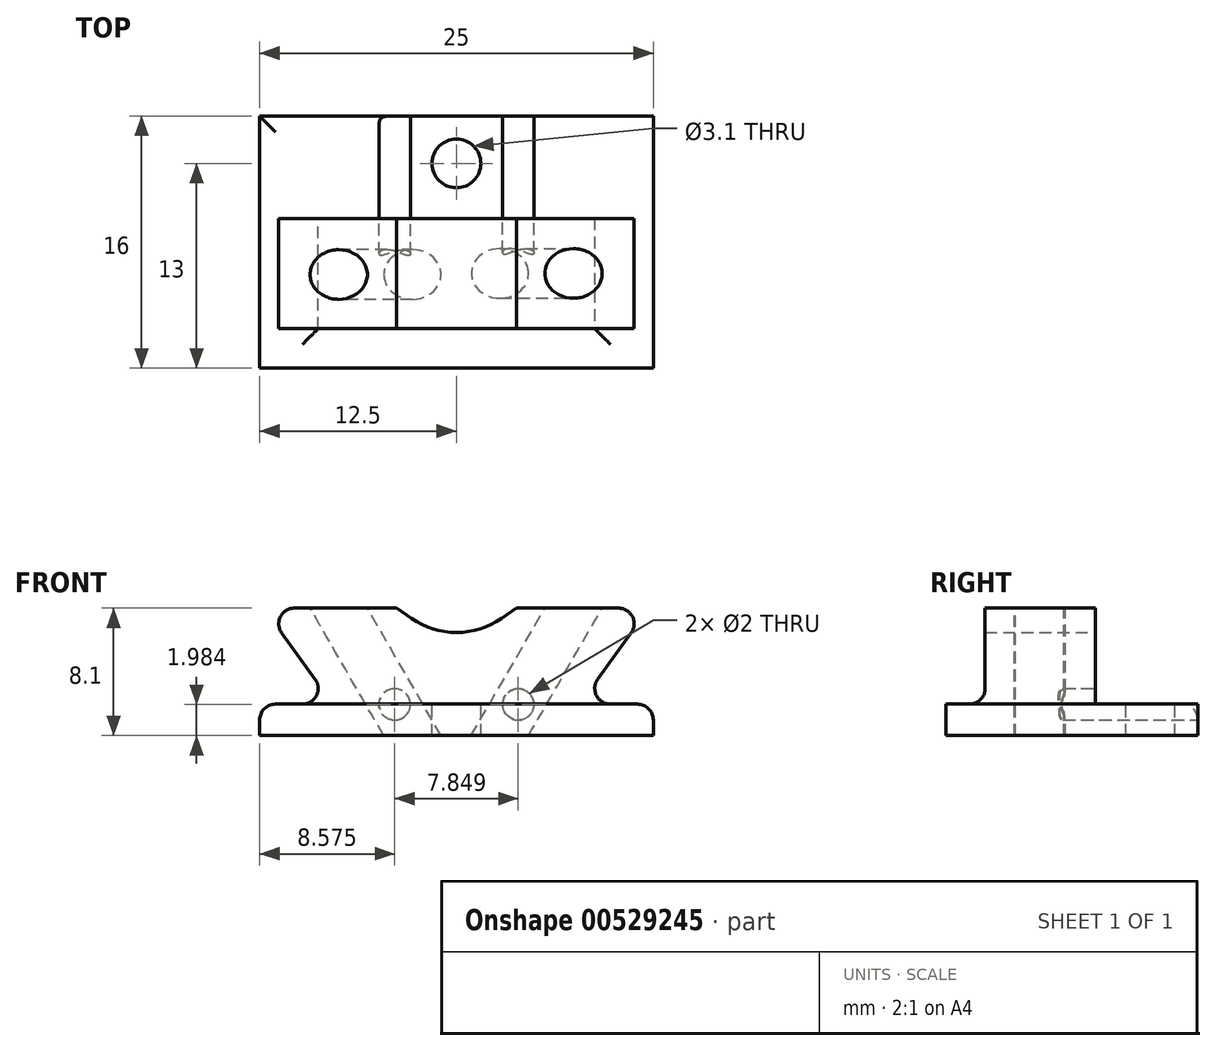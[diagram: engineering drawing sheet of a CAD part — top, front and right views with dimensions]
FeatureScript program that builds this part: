
annotation { "Feature Type Name" : "Feature", "Feature Type Description" : "" }
export const myFeature = defineFeature(function(context is Context, id is Id, definition is map)
    precondition{}
    {
        {
            var Q0;
            Q0=qCreatedBy(makeId("Front.planeOp"),FACE);
            cPlane(context, id + "F0", {"entities" : qUnion([Q0]), "cplaneType" : CPlaneType.OFFSET, "offset" : 2 * mm, "width" : 150 * mm, "height" : 150 * mm});
        }
        {
            var Q0;
            Q0=qCreatedBy(makeId("Top.planeOp"),FACE);
            var sketch = newSketch(context, id + "F1", { "sketchPlane" : qUnion([Q0])});
            skLineSegment(sketch, "E0.rect.bottom", {"start": v(12.5, -8) * mm, "end": v(-12.5, -8) * mm});
            skLineSegment(sketch, "E0.rect.top", {"start": v(12.5, 8) * mm, "end": v(-12.5, 8) * mm});
            skLineSegment(sketch, "E0.rect.left", {"start": v(12.5, -8) * mm, "end": v(12.5, 8) * mm});
            skLineSegment(sketch, "E0.rect.right", {"start": v(-12.5, -8) * mm, "end": v(-12.5, 8) * mm});
            skPoint(sketch, "E0.rect.middle", {"position": v(0, 0) * mm});
            skSolve(sketch);
        }
        {
            var Q0;
            Q0=makeQuery(id+"F1.imprint","IMPRINT",FACE,{"disambiguationData":[TD([[makeQuery(id+"F1.imprint","IMPRINT",EDGE,{"derivedFrom":sQuery(id+"F1.wireOp",EDGE,"E0.rect.bottom")}),-1.0]])]});
            extrude(context, id + "F2", {"entities" : qUnion([Q0]), "depth" : 2 * mm});
        }
        {
            var Q0;
            Q0=makeQuery(id+"F2.opExtrude","CAP_FACE",FACE,{"disambiguationData":[OSD([sQuery(id+"F1.wireOp",EDGE,"E0.rect.bottom"),sQuery(id+"F1.wireOp",EDGE,"E0.rect.top"),sQuery(id+"F1.wireOp",EDGE,"E0.rect.left"),sQuery(id+"F1.wireOp",EDGE,"E0.rect.right")])],"isStart":false});
            var sketch = newSketch(context, id + "F3", { "sketchPlane" : qUnion([Q0])});
            skLineSegment(sketch, "E1", {"start": v(-17.25, 5) * mm, "end": v(20.16, 5) * mm, "construction": true});
            skCircle(sketch, "E2", {"center": v(0, 5) * mm, "radius": 1.55 * mm});
            skSolve(sketch);
        }
        {
            var Q0;
            Q0=makeQuery(id+"F3.imprint","IMPRINT",FACE,{"disambiguationData":[TD([[makeQuery(id+"F3.imprint","IMPRINT",EDGE,{"derivedFrom":sQuery(id+"F3.wireOp",EDGE,"E2")}),1.0]])]});
            extrude(context, id + "F4", {"entities" : qUnion([Q0]), "operationType" : NewBodyOperationType.REMOVE, "endBound" : BoundingType.THROUGH_ALL, "oppositeDirection" : true, "depth" : 25 * mm});
        }
        {
            var Q0;
            Q0=qCreatedBy(id+"F0.planeOp",FACE);
            var sketch = newSketch(context, id + "F5", { "sketchPlane" : qUnion([Q0])});
            skLineSegment(sketch, "E3", {"start": v(-12.25, 8.1) * mm, "end": v(-3.8, 8.1) * mm});
            skLineSegment(sketch, "E4", {"start": v(-3.8, 8.1) * mm, "end": v(-2.87, 7.45) * mm});
            skLineSegment(sketch, "E5", {"start": v(2.87, 7.45) * mm, "end": v(3.8, 8.1) * mm});
            skLineSegment(sketch, "E6", {"start": v(3.8, 8.1) * mm, "end": v(12.25, 8.1) * mm});
            skLineSegment(sketch, "E7", {"start": v(-12.25, 8.1) * mm, "end": v(-6.37, 0) * mm});
            skLineSegment(sketch, "E8", {"start": v(6.37, 0) * mm, "end": v(12.25, 8.1) * mm});
            skLineSegment(sketch, "E9", {"start": v(-6.37, 0) * mm, "end": v(6.37, 0) * mm});
            skPoint(sketch, "E10.orphan", {"position": v(0, -8.79) * mm});
            skPoint(sketch, "E11.visualSharp", {"position": v(0, 5.44) * mm});
            skArc(sketch, "E11.filletArc", {"start": v(-2.87, 7.45) * mm, "mid": v(0, 6.55) * mm, "end": v(2.87, 7.45) * mm});
            skSolve(sketch);
        }
        {
            var Q0;
            Q0=qSketchRegion(id+"F5",true);
            extrude(context, id + "F6", {"entities" : qUnion([Q0]), "operationType" : NewBodyOperationType.ADD, "endBound" : BoundingType.SYMMETRIC, "depth" : 7 * mm});
        }
        {
            var Q0;
            Q0=qCreatedBy(id+"F0.planeOp",FACE);
            var sketch = newSketch(context, id + "F7", { "sketchPlane" : qUnion([Q0])});
            skLineSegment(sketch, "E12", {"start": v(-10, 12.55) * mm, "end": v(0, -4.77) * mm, "construction": true});
            skLineSegment(sketch, "E13", {"start": v(0, -4.77) * mm, "end": v(10, 12.55) * mm, "construction": true});
            skLineSegment(sketch, "E14", {"start": v(10, 12.55) * mm, "end": v(-10, 12.55) * mm, "construction": true});
            skSolve(sketch);
        }
        {
            var Q0;
            Q0=sQuery(id+"F7.wireOp",VERTEX,"E14.start");
            var Q1;
            Q1=sQuery(id+"F7.wireOp",EDGE,"E13");
            cPlane(context, id + "F8", {"entities" : qUnion([Q0, Q1]), "cplaneType" : CPlaneType.LINE_POINT, "offset" : 150 * mm, "width" : 150 * mm, "height" : 150 * mm});
        }
        {
            var Q0;
            Q0=qCreatedBy(id+"F8.planeOp",FACE);
            var sketch = newSketch(context, id + "F9", { "sketchPlane" : qUnion([Q0])});
            skCircle(sketch, "E15", {"center": v(2.39, -2) * mm, "radius": 1.57 * mm});
            skSolve(sketch);
        }
        {
            var Q0;
            Q0=qSketchRegion(id+"F9",true);
            extrude(context, id + "F10", {"entities" : qUnion([Q0]), "operationType" : NewBodyOperationType.REMOVE, "oppositeDirection" : true, "depth" : 25 * mm});
        }
        {
            var Q0;
            Q0=sQuery(id+"F7.wireOp",EDGE,"E12");
            var Q1;
            Q1=sQuery(id+"F7.wireOp",VERTEX,"E14.end");
            cPlane(context, id + "F11", {"entities" : qUnion([Q0, Q1]), "cplaneType" : CPlaneType.LINE_POINT, "offset" : 150 * mm, "width" : 150 * mm, "height" : 150 * mm});
        }
        {
            var Q0;
            Q0=qCreatedBy(id+"F11.planeOp",FACE);
            var sketch = newSketch(context, id + "F12", { "sketchPlane" : qUnion([Q0])});
            skCircle(sketch, "E16", {"center": v(-2.42, 2.06) * mm, "radius": 1.57 * mm});
            skSolve(sketch);
        }
        {
            var Q0;
            Q0=qSketchRegion(id+"F12",true);
            extrude(context, id + "F13", {"entities" : qUnion([Q0]), "operationType" : NewBodyOperationType.REMOVE, "endBound" : BoundingType.THROUGH_ALL, "depth" : 25 * mm});
        }
        {
            var Q0;
            Q0=makeQuery(id+"F2.opExtrude","SWEPT_FACE",FACE,{"disambiguationData":[OSD([sQuery(id+"F1.wireOp",EDGE,"E0.rect.top")])]});
            var sketch = newSketch(context, id + "F14", { "sketchPlane" : qUnion([Q0])});
            skCircle(sketch, "E17", {"center": v(3.92, 1.98) * mm, "radius": 1 * mm});
            skCircle(sketch, "E18.0.MirrorC", {"center": v(-3.92, 1.98) * mm, "radius": 1 * mm});
            skSolve(sketch);
        }
        {
            var Q0;
            Q0=qSketchRegion(id+"F14",true);
            var Q1;
            Q1=qCreatedBy(id+"F0.planeOp",FACE);
            extrude(context, id + "F15", {"entities" : qUnion([Q0]), "operationType" : NewBodyOperationType.REMOVE, "endBound" : BoundingType.UP_TO_SURFACE, "oppositeDirection" : true, "endBoundEntityFace" : qUnion([Q1]), "depth" : 25 * mm});
        }
        {
            var Q0;
            Q0=makeQuery(id+"F6.boolean.opBoolean","INTERSECT",EDGE,{"derivedFrom":[makeQuery(id+"F2.opExtrude","CAP_FACE",FACE,{"disambiguationData":[OSD([sQuery(id+"F1.wireOp",EDGE,"E0.rect.bottom"),sQuery(id+"F1.wireOp",EDGE,"E0.rect.top"),sQuery(id+"F1.wireOp",EDGE,"E0.rect.left"),sQuery(id+"F1.wireOp",EDGE,"E0.rect.right")])],"isStart":false}),makeQuery(id+"F6.opExtrude","CAP_FACE",FACE,{"disambiguationData":[OSD([sQuery(id+"F5.wireOp",EDGE,"E3"),sQuery(id+"F5.wireOp",EDGE,"E4"),sQuery(id+"F5.wireOp",EDGE,"E5"),sQuery(id+"F5.wireOp",EDGE,"E6"),sQuery(id+"F5.wireOp",EDGE,"E7"),sQuery(id+"F5.wireOp",EDGE,"E8"),sQuery(id+"F5.wireOp",EDGE,"E9"),sQuery(id+"F5.wireOp",EDGE,"E11.filletArc")])],"isStart":false})]});
            var Q1;
            Q1=makeQuery(id+"F6.boolean.opBoolean","INTERSECT",EDGE,{"derivedFrom":[makeQuery(id+"F2.opExtrude","CAP_FACE",FACE,{"disambiguationData":[OSD([sQuery(id+"F1.wireOp",EDGE,"E0.rect.bottom"),sQuery(id+"F1.wireOp",EDGE,"E0.rect.top"),sQuery(id+"F1.wireOp",EDGE,"E0.rect.left"),sQuery(id+"F1.wireOp",EDGE,"E0.rect.right")])],"isStart":false}),makeQuery(id+"F6.opExtrude","SWEPT_FACE",FACE,{"disambiguationData":[OSD([sQuery(id+"F5.wireOp",EDGE,"E8")])]})]});
            var Q2;
            Q2=makeQuery(id+"F6.boolean.opBoolean","INTERSECT",EDGE,{"derivedFrom":[makeQuery(id+"F2.opExtrude","CAP_FACE",FACE,{"disambiguationData":[OSD([sQuery(id+"F1.wireOp",EDGE,"E0.rect.bottom"),sQuery(id+"F1.wireOp",EDGE,"E0.rect.top"),sQuery(id+"F1.wireOp",EDGE,"E0.rect.left"),sQuery(id+"F1.wireOp",EDGE,"E0.rect.right")])],"isStart":false}),makeQuery(id+"F6.opExtrude","SWEPT_FACE",FACE,{"disambiguationData":[OSD([sQuery(id+"F5.wireOp",EDGE,"E7")])]})]});
            var Q3;
            Q3=makeQuery(id+"F6.opExtrude","SWEPT_EDGE",EDGE,{"disambiguationData":[OSD([sQuery(id+"F5.wireOp",EDGE,"E6"),sQuery(id+"F5.wireOp",EDGE,"E8")])]});
            var Q4;
            Q4=makeQuery(id+"F6.opExtrude","SWEPT_EDGE",EDGE,{"disambiguationData":[OSD([sQuery(id+"F5.wireOp",EDGE,"E3"),sQuery(id+"F5.wireOp",EDGE,"E7")])]});
            var Q5;
            Q5=makeQuery(id+"F2.opExtrude","CAP_EDGE",EDGE,{"disambiguationData":[OSD([sQuery(id+"F1.wireOp",EDGE,"E0.rect.left")])],"isStart":false});
            var Q6;
            Q6=makeQuery(id+"F2.opExtrude","CAP_EDGE",EDGE,{"disambiguationData":[OSD([sQuery(id+"F1.wireOp",EDGE,"E0.rect.right")])],"isStart":false});
            var Q7;
            {var subQ0=sQuery(id+"F1.wireOp",EDGE,"E0.rect.top");var subQ1=sQuery(id+"F1.wireOp",EDGE,"E0.rect.right");Q7=makeQuery(id+"F15.boolean.opBoolean","SPLIT",EDGE,{"disambiguationData":[TD([makeQuery(id+"F2.opExtrude","CAP_FACE",FACE,{"disambiguationData":[OSD([sQuery(id+"F1.wireOp",EDGE,"E0.rect.bottom"),subQ0,sQuery(id+"F1.wireOp",EDGE,"E0.rect.left"),subQ1])],"isStart":false}),makeQuery(id+"F2.opExtrude","SWEPT_FACE",FACE,{"disambiguationData":[OSD([subQ0])]}),makeQuery(id+"F2.opExtrude","SWEPT_FACE",FACE,{"disambiguationData":[OSD([subQ1])]}),makeQuery(id+"F15.opExtrude","SWEPT_FACE",FACE,{"disambiguationData":[OSD([sQuery(id+"F14.wireOp",EDGE,"E17")])]})])],"derivedFrom":makeQuery(id+"F2.opExtrude","CAP_EDGE",EDGE,{"disambiguationData":[OSD([subQ0])],"isStart":false})});}
            fillet(context, id + "F16", {"entities" : qUnion([Q0, Q1, Q2, Q3, Q4, Q5, Q6, Q7]), "radius" : 1 * mm, "tangentPropagation" : true, "allowEdgeOverflow" : false});
        }
    });
